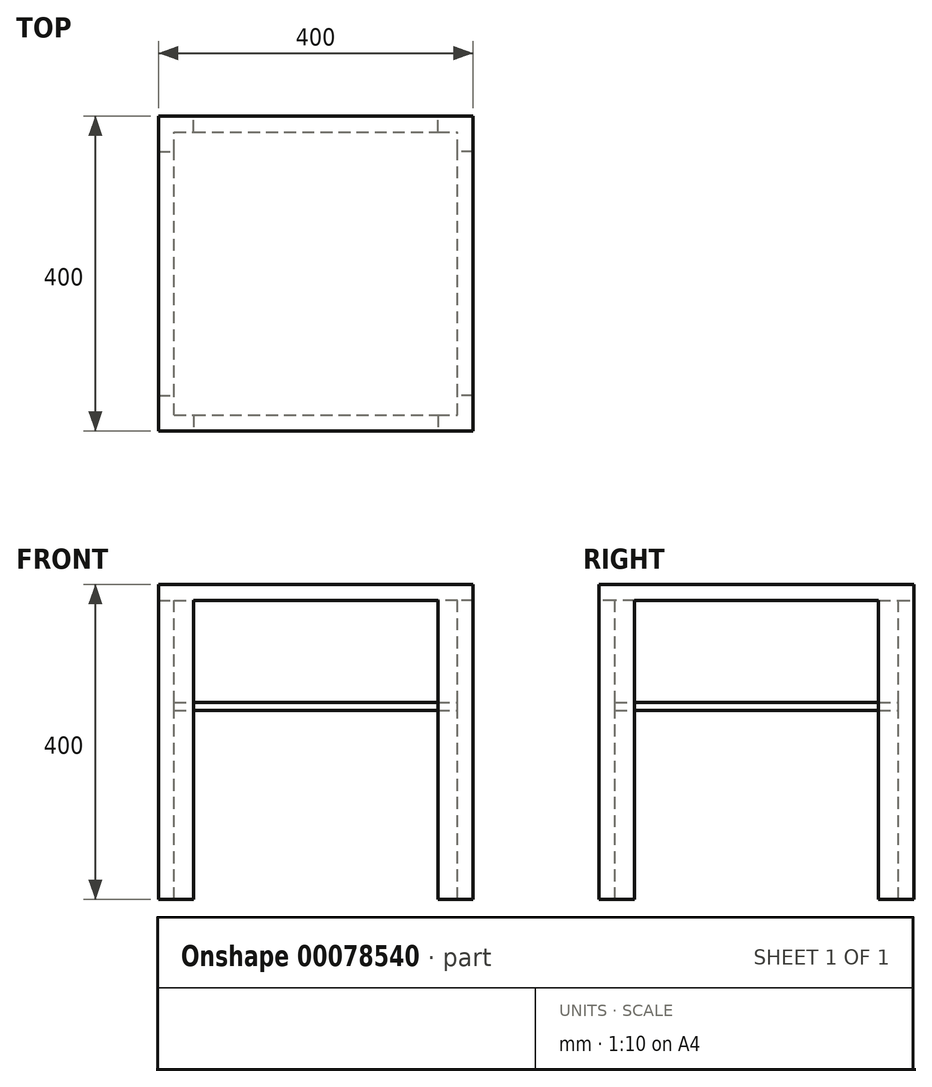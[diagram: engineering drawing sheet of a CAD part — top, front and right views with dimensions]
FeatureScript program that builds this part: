
annotation { "Feature Type Name" : "Feature", "Feature Type Description" : "" }
export const myFeature = defineFeature(function(context is Context, id is Id, definition is map)
    precondition{}
    {
        {
            var Q0;
            Q0=qCreatedBy(makeId("Top.planeOp"),FACE);
            cPlane(context, id + "F0", {"entities" : qUnion([Q0]), "cplaneType" : CPlaneType.OFFSET, "offset" : 400 * mm, "width" : 152.4 * mm, "height" : 152.4 * mm});
        }
        {
            var Q0;
            Q0=qCreatedBy(id+"F0.planeOp",FACE);
            var sketch = newSketch(context, id + "F1", { "sketchPlane" : qUnion([Q0])});
            skLineSegment(sketch, "E0.bottom", {"start": v(-200, 200) * mm, "end": v(200, 200) * mm});
            skLineSegment(sketch, "E0.top", {"start": v(-200, -200) * mm, "end": v(200, -200) * mm});
            skLineSegment(sketch, "E0.left", {"start": v(-200, 200) * mm, "end": v(-200, -200) * mm});
            skLineSegment(sketch, "E0.right", {"start": v(200, 200) * mm, "end": v(200, -200) * mm});
            skSolve(sketch);
        }
        {
            var Q0;
            Q0 = qSketchRegion(id + "F1", true);
            extrude(context, id + "F2", {"entities" : qUnion([Q0]), "oppositeDirection" : true, "depth" : 20 * mm});
        }
        {
            var Q0;
            Q0=makeQuery(id+"F2.opExtrude","CAP_FACE",FACE,{"disambiguationData":[OSD([sQuery(id+"F1.wireOp",EDGE,"E0.bottom"),sQuery(id+"F1.wireOp",EDGE,"E0.top"),sQuery(id+"F1.wireOp",EDGE,"E0.left"),sQuery(id+"F1.wireOp",EDGE,"E0.right")])],"isStart":false});
            var sketch = newSketch(context, id + "F3", { "sketchPlane" : qUnion([Q0])});
            skLineSegment(sketch, "E1", {"start": v(-200, 200) * mm, "end": v(-200, 155) * mm});
            skLineSegment(sketch, "E2", {"start": v(-200, 155) * mm, "end": v(-180, 155) * mm});
            skLineSegment(sketch, "E3", {"start": v(-180, 155) * mm, "end": v(-180, 180) * mm});
            skLineSegment(sketch, "E4", {"start": v(-180, 180) * mm, "end": v(-155, 180) * mm});
            skLineSegment(sketch, "E5", {"start": v(-155, 180) * mm, "end": v(-155, 200) * mm});
            skLineSegment(sketch, "E6", {"start": v(-155, 200) * mm, "end": v(-200, 200) * mm});
            skLineSegment(sketch, "E7.MirrorCS", {"start": v(180, 180) * mm, "end": v(155, 180) * mm});
            skLineSegment(sketch, "E8.MirrorCS", {"start": v(155, 180) * mm, "end": v(155, 200) * mm});
            skLineSegment(sketch, "E9.MirrorCS", {"start": v(155, 200) * mm, "end": v(200, 200) * mm});
            skLineSegment(sketch, "E10.MirrorCS", {"start": v(200, 200) * mm, "end": v(200, 155) * mm});
            skLineSegment(sketch, "E11.MirrorCS", {"start": v(200, 155) * mm, "end": v(180, 155) * mm});
            skLineSegment(sketch, "E12.MirrorCS", {"start": v(180, 155) * mm, "end": v(180, 180) * mm});
            skLineSegment(sketch, "E13.MirrorCS", {"start": v(200, -155) * mm, "end": v(180, -155) * mm});
            skLineSegment(sketch, "E14.MirrorCS", {"start": v(200, -200) * mm, "end": v(200, -155) * mm});
            skLineSegment(sketch, "E15.MirrorCS", {"start": v(155, -200) * mm, "end": v(200, -200) * mm});
            skLineSegment(sketch, "E16.MirrorCS", {"start": v(155, -180) * mm, "end": v(155, -200) * mm});
            skLineSegment(sketch, "E17.MirrorCS", {"start": v(180, -180) * mm, "end": v(155, -180) * mm});
            skLineSegment(sketch, "E18.MirrorCS", {"start": v(180, -155) * mm, "end": v(180, -180) * mm});
            skLineSegment(sketch, "E19.MirrorCS", {"start": v(-180, -155) * mm, "end": v(-180, -180) * mm});
            skLineSegment(sketch, "E20.MirrorCS", {"start": v(-200, -155) * mm, "end": v(-180, -155) * mm});
            skLineSegment(sketch, "E21.MirrorCS", {"start": v(-200, -200) * mm, "end": v(-200, -155) * mm});
            skLineSegment(sketch, "E22.MirrorCS", {"start": v(-155, -180) * mm, "end": v(-155, -200) * mm});
            skLineSegment(sketch, "E23.MirrorCS", {"start": v(-180, -180) * mm, "end": v(-155, -180) * mm});
            skLineSegment(sketch, "E24.MirrorCS", {"start": v(-155, -200) * mm, "end": v(-200, -200) * mm});
            skSolve(sketch);
        }
        {
            var Q0;
            Q0 = qSketchRegion(id + "F3", true);
            var Q1;
            Q1=qCreatedBy(makeId("Top.planeOp"),FACE);
            extrude(context, id + "F4", {"entities" : qUnion([Q0]), "operationType" : NewBodyOperationType.ADD, "endBound" : BoundingType.UP_TO_SURFACE, "endBoundEntityFace" : qUnion([Q1]), "depth" : 25 * mm});
        }
        {
            var Q0;
            Q0=qCreatedBy(makeId("Top.planeOp"),FACE);
            cPlane(context, id + "F5", {"entities" : qUnion([Q0]), "cplaneType" : CPlaneType.OFFSET, "offset" : 250 * mm, "width" : 150 * mm, "height" : 150 * mm});
        }
        {
            var Q0;
            Q0=qCreatedBy(id+"F5.planeOp",FACE);
            var sketch = newSketch(context, id + "F6", { "sketchPlane" : qUnion([Q0])});
            skLineSegment(sketch, "E25.bottom", {"start": v(-180, -180) * mm, "end": v(180, -180) * mm});
            skLineSegment(sketch, "E25.top", {"start": v(-180, 180) * mm, "end": v(180, 180) * mm});
            skLineSegment(sketch, "E25.left", {"start": v(-180, -180) * mm, "end": v(-180, 180) * mm});
            skLineSegment(sketch, "E25.right", {"start": v(180, -180) * mm, "end": v(180, 180) * mm});
            skSolve(sketch);
        }
        {
            var Q0;
            Q0=makeQuery(id+"F6.imprint","IMPRINT",FACE,{"disambiguationData":[TD([[makeQuery(id+"F6.imprint","IMPRINT",EDGE,{"derivedFrom":sQuery(id+"F6.wireOp",EDGE,"E25.bottom")}),1.0]])]});
            extrude(context, id + "F7", {"entities" : qUnion([Q0]), "operationType" : NewBodyOperationType.ADD, "oppositeDirection" : true, "depth" : 10 * mm});
        }
    });
